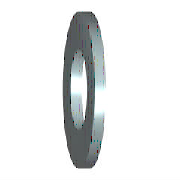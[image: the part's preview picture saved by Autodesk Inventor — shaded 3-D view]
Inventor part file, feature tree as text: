
AUTODESK INVENTOR PART (.ipt)
format: ipt  version: 2021 (Build 250183000, 183)  size: 106,496 bytes
history: native  units: mm (DEFAULTED — no unit token found)
features: other x1, plane x1, sketch x1
ambient origin geometry x7: Origin, YZ Plane, XY Plane, X Axis, Y Axis, Z Axis, Center Point
bodies: Solid1 (feature_tree), Body (feature_tree)
feature tree (3):
  other  "Work Axis1"
  plane  "Work Plane1"
  sketch  "Sketch"  dims[d0=3.2mm d1=7.0mm d2=0.5mm d3=0.0mm d4=0.0mm d5=0.0mm d6=0.0mm d7=0.0mm]
